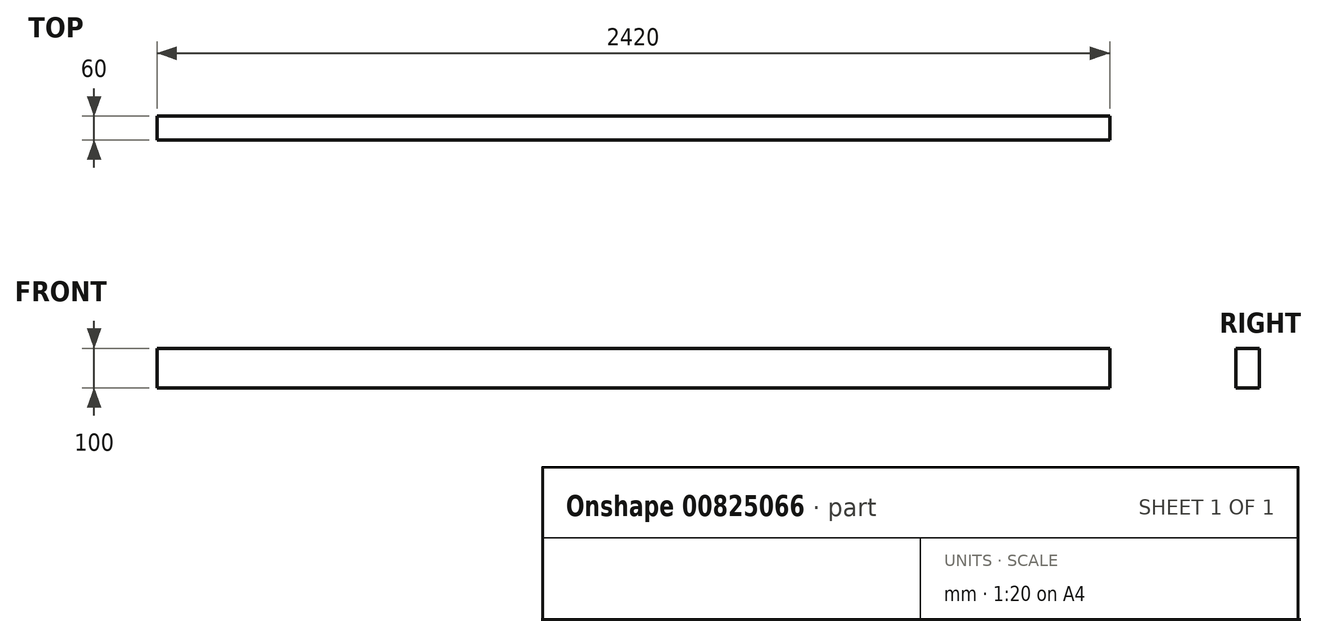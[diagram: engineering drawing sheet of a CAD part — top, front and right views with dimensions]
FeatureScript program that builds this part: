
annotation { "Feature Type Name" : "Feature", "Feature Type Description" : "" }
export const myFeature = defineFeature(function(context is Context, id is Id, definition is map)
    precondition{}
    {
        {
            var Q0;
            Q0=qCreatedBy(makeId("Top.planeOp"),FACE);
            var sketch = newSketch(context, id + "F0", { "sketchPlane" : qUnion([Q0])});
            skLineSegment(sketch, "E0.bottom", {"start": v(-1222.6, 10.5) * mm, "end": v(1197.4, 10.5) * mm});
            skLineSegment(sketch, "E0.top", {"start": v(-1222.6, -49.5) * mm, "end": v(1197.4, -49.5) * mm});
            skLineSegment(sketch, "E0.left", {"start": v(-1222.6, 10.5) * mm, "end": v(-1222.6, -49.5) * mm});
            skLineSegment(sketch, "E0.right", {"start": v(1197.4, 10.5) * mm, "end": v(1197.4, -49.5) * mm});
            skSolve(sketch);
        }
        {
            var Q0;
            Q0=makeQuery(id+"F0.imprint","IMPRINT",FACE,{"disambiguationData":[TD([[makeQuery(id+"F0.imprint","IMPRINT",EDGE,{"derivedFrom":sQuery(id+"F0.wireOp",EDGE,"E0.bottom")}),-1.0]])]});
            extrude(context, id + "F1", {"entities" : qUnion([Q0]), "depth" : 100 * mm, "offsetDistance" : 25 * mm});
        }
    });
